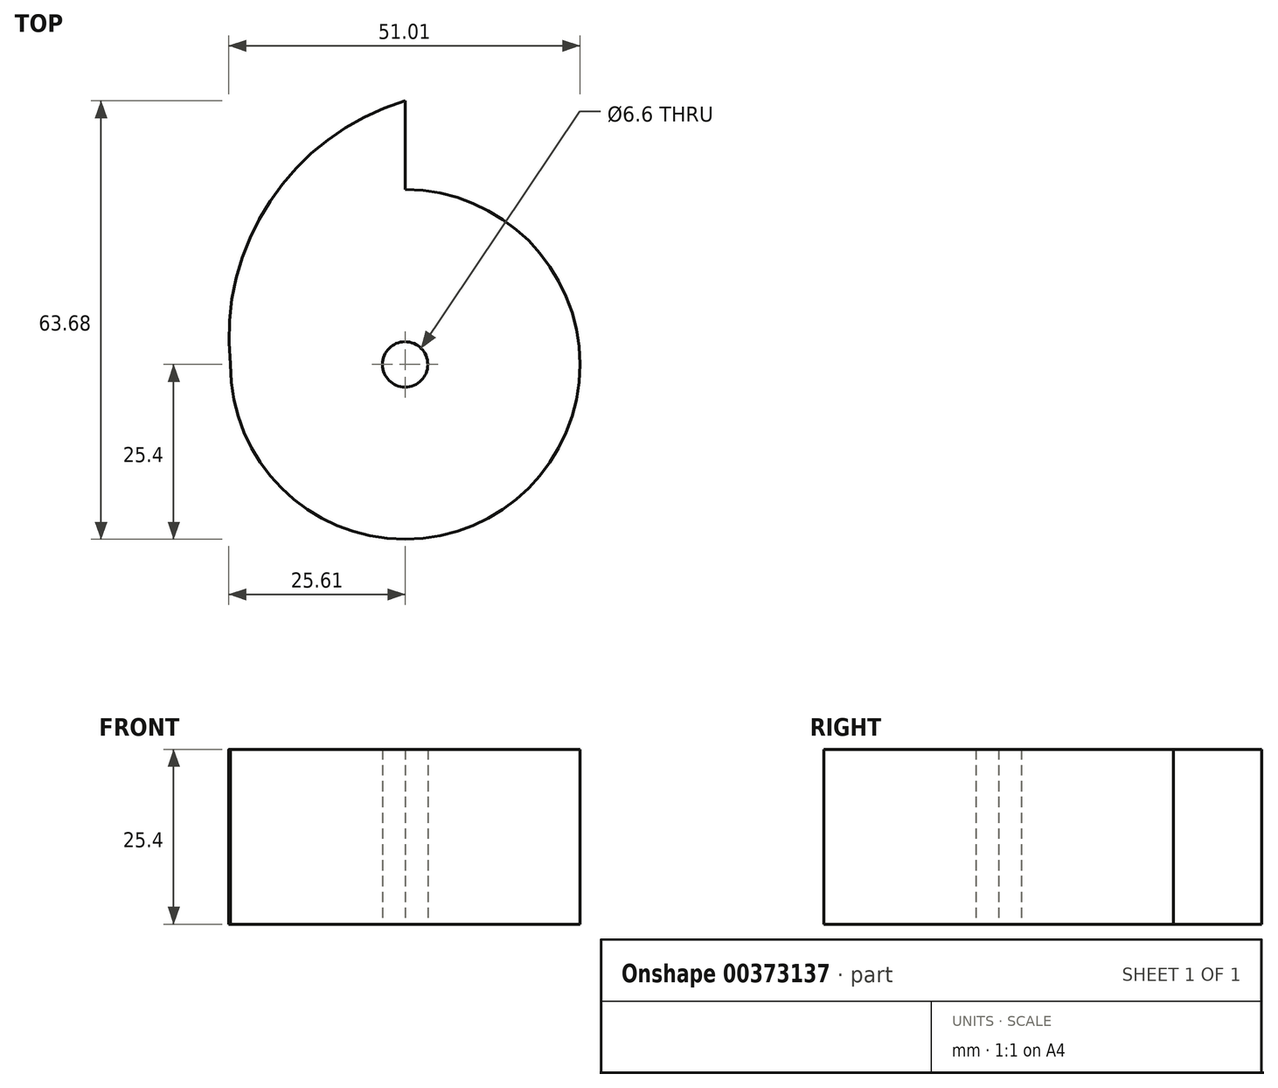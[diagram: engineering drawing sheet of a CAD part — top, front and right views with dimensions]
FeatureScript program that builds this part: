
annotation { "Feature Type Name" : "Feature", "Feature Type Description" : "" }
export const myFeature = defineFeature(function(context is Context, id is Id, definition is map)
    precondition{}
    {
        {
            var Q0;
            Q0=qCreatedBy(makeId("Top.planeOp"),FACE);
            var sketch = newSketch(context, id + "F0", { "sketchPlane" : qUnion([Q0])});
            skCircle(sketch, "E0", {"center": v(0, 0) * mm, "radius": 25.4 * mm});
            skLineSegment(sketch, "E1", {"start": v(0, 25.4) * mm, "end": v(0, 38.28) * mm});
            skArc(sketch, "E2", {"start": v(0, 38.28) * mm, "mid": v(-19.62, 23.73) * mm, "end": v(-25.4, 0) * mm});
            skCircle(sketch, "E3", {"center": v(0, 0) * mm, "radius": 3.3 * mm});
            skSolve(sketch);
        }
        {
            var Q0;
            {var subQ0=sQuery(id+"F0.wireOp",EDGE,"E0");var subQ1=makeQuery(id+"F0.imprint","INTERSECT",VERTEX,{"derivedFrom":[subQ0,sQuery(id+"F0.wireOp",EDGE,"E1")]});Q0=makeQuery(id+"F0.imprint","IMPRINT",FACE,{"disambiguationData":[TD([[makeQuery(id+"F0.imprint","IMPRINT",EDGE,{"disambiguationData":[TD([[subQ1,-1.0]])],"derivedFrom":subQ0}),1.0]])]});}
            var Q1;
            {var subQ0=sQuery(id+"F0.wireOp",EDGE,"E1");Q1=makeQuery(id+"F0.imprint","IMPRINT",FACE,{"disambiguationData":[TD([[makeQuery(id+"F0.imprint","IMPRINT",EDGE,{"derivedFrom":subQ0}),1.0]])]});}
            extrude(context, id + "F1", {"entities" : qUnion([Q0, Q1]), "depth" : 25.4 * mm});
        }
    });
